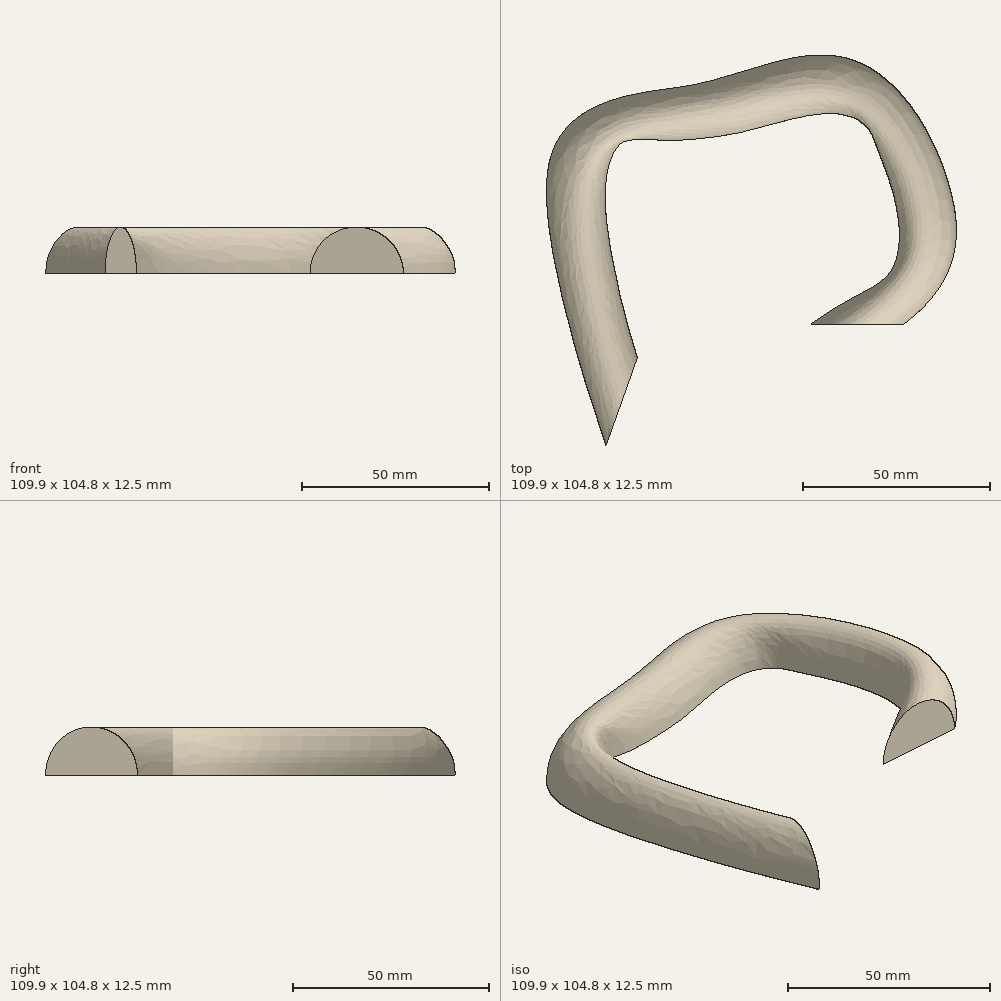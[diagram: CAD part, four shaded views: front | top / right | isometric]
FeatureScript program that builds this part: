
annotation { "Feature Type Name" : "Feature", "Feature Type Description" : "" }
export const myFeature = defineFeature(function(context is Context, id is Id, definition is map)
    precondition{}
    {
        {
            var Q0;
            Q0=qCreatedBy(makeId("Front.planeOp"),FACE);
            var sketch = newSketch(context, id + "F0", { "sketchPlane" : qUnion([Q0])});
            skArc(sketch, "E0", {"start": v(12.5, 0) * mm, "mid": v(0, 12.5) * mm, "end": v(-12.5, 0) * mm});
            skLineSegment(sketch, "E1", {"start": v(-12.5, 0) * mm, "end": v(12.5, 0) * mm});
            skSolve(sketch);
        }
        {
            var Q0;
            Q0=qCreatedBy(makeId("Top.planeOp"),FACE);
            var sketch = newSketch(context, id + "F1", { "sketchPlane" : qUnion([Q0])});
            skFitSpline(sketch, "E2", {"points": [v(0, 0) * mm, v(17.09, 22.22) * mm, v(0, 60.15) * mm, v(-36.91, 58.1) * mm, v(-70.75, 46.48) * mm, v(-71.43, 8.54) * mm, v(-63.23, -20.85) * mm], "startDerivative": vector(157.87, 119.8) * mm, "endDerivative": vector(54.1, -170.84) * mm});
            skSolve(sketch);
        }
        {
            var Q0;
            Q0=makeQuery(id+"F0.imprint","IMPRINT",FACE,{"disambiguationData":[TD([[makeQuery(id+"F0.imprint","IMPRINT",EDGE,{"derivedFrom":sQuery(id+"F0.wireOp",EDGE,"E0")}),1.0]])]});
            var Q1;
            Q1=sQuery(id+"F1.wireOp",EDGE,"E2");
            sweep(context, id + "F2", {"profiles" : qUnion([Q0]), "path" : qUnion([Q1])});
        }
    });
